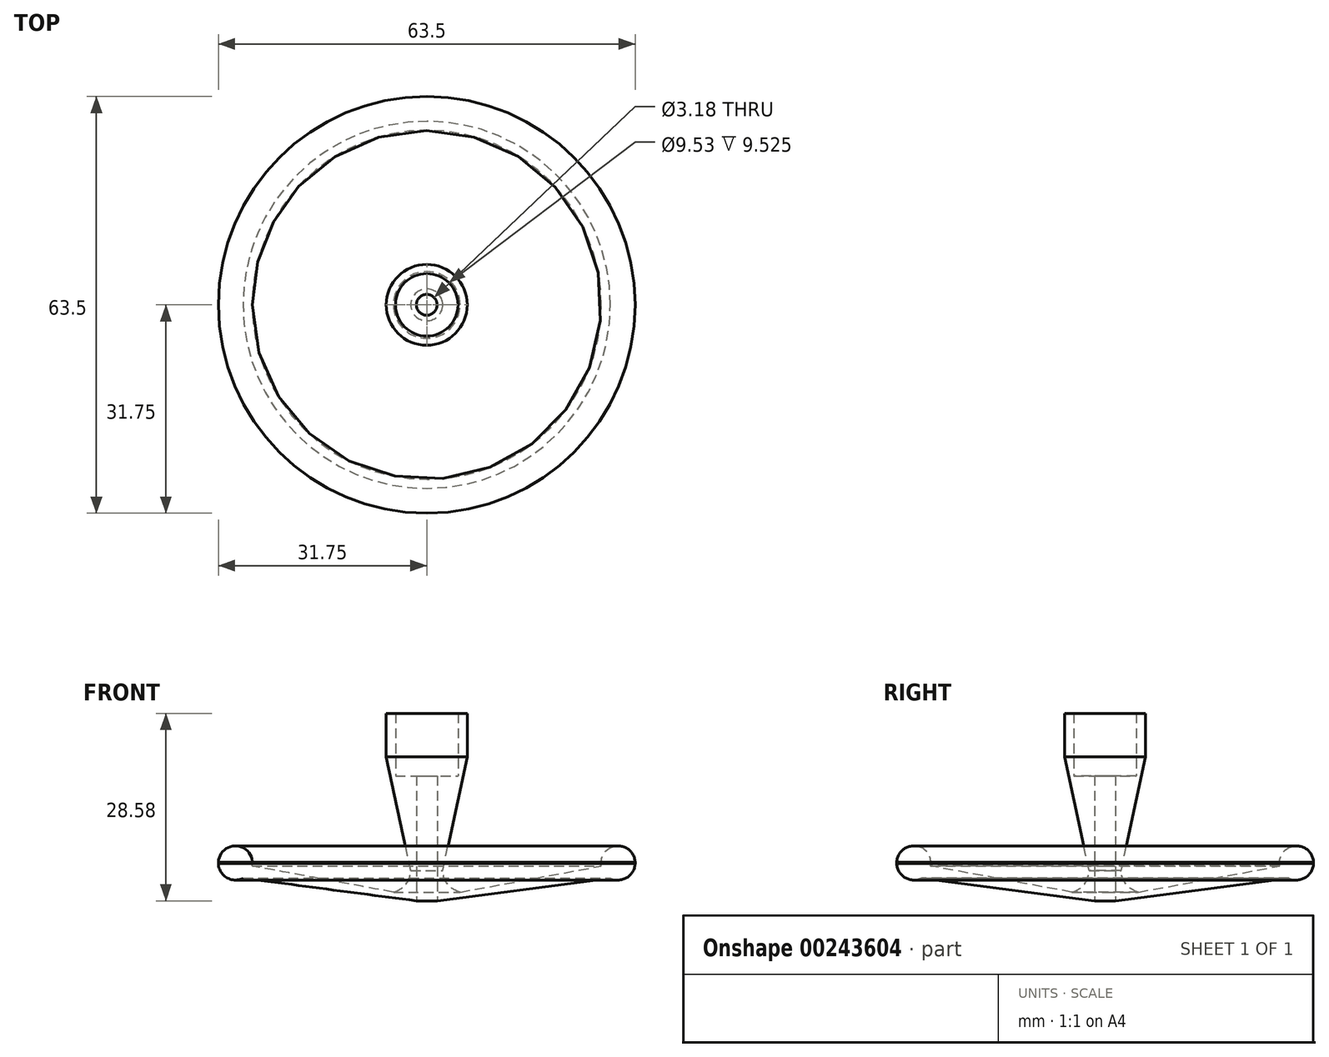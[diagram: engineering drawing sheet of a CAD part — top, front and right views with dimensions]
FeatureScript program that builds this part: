
annotation { "Feature Type Name" : "Feature", "Feature Type Description" : "" }
export const myFeature = defineFeature(function(context is Context, id is Id, definition is map)
    precondition{}
    {
        {
            var Q0;
            Q0=qCreatedBy(makeId("Front.planeOp"),FACE);
            var sketch = newSketch(context, id + "F0", { "sketchPlane" : qUnion([Q0])});
            skLineSegment(sketch, "E0.top", {"start": v(4.76, 28.58) * mm, "end": v(6.17, 28.58) * mm});
            skLineSegment(sketch, "E0.right", {"start": v(31.75, 5.66) * mm, "end": v(31.75, 5.89) * mm});
            skLineSegment(sketch, "E1.top", {"start": v(1.59, 19.05) * mm, "end": v(4.76, 19.05) * mm});
            skLineSegment(sketch, "E1.right", {"start": v(4.76, 28.58) * mm, "end": v(4.76, 19.05) * mm});
            skPoint(sketch, "E2.oppositeSnap0", {"position": v(2.38, 19.05) * mm});
            skLineSegment(sketch, "E3.bottom", {"start": v(2.38, 15.49) * mm, "end": v(2.38, 15.49) * mm});
            skLineSegment(sketch, "E3.top", {"start": v(2.38, 19.05) * mm, "end": v(2.38, 19.05) * mm});
            skLineSegment(sketch, "E4", {"start": v(1.59, 7.42) * mm, "end": v(1.59, 19.05) * mm});
            skLineSegment(sketch, "E5", {"start": v(1.59, 19.05) * mm, "end": v(1.59, 0) * mm});
            skPoint(sketch, "E1.left.end.orphan", {"position": v(0, 19.05) * mm});
            skPoint(sketch, "E6.end.orphan", {"position": v(1.59, 0.68) * mm});
            skPoint(sketch, "E7.end.orphan", {"position": v(27.94, 8.1) * mm});
            skLineSegment(sketch, "E8", {"start": v(6.17, 28.58) * mm, "end": v(6.17, 21.95) * mm});
            skLineSegment(sketch, "E9", {"start": v(6.17, 21.95) * mm, "end": v(2.43, 4.6) * mm});
            skPoint(sketch, "E10.end.orphan", {"position": v(30.36, 8.1) * mm});
            skArc(sketch, "E11", {"start": v(27.97, 3.46) * mm, "mid": v(31.2, 7.39) * mm, "end": v(26.62, 5.17) * mm});
            skPoint(sketch, "E11.first.point", {"position": v(31.75, 5.89) * mm});
            skPoint(sketch, "E11.second.point", {"position": v(26.62, 5.17) * mm});
            skPoint(sketch, "E11.third.point", {"position": v(27.97, 3.46) * mm});
            skLineSegment(sketch, "E12", {"start": v(1.59, 0) * mm, "end": v(27.97, 3.46) * mm});
            skLineSegment(sketch, "E13", {"start": v(5.08, 1.33) * mm, "end": v(26.6, 5.3) * mm});
            skArc(sketch, "E14", {"start": v(2.43, 4.6) * mm, "mid": v(3.2, 2.52) * mm, "end": v(5.08, 1.33) * mm});
            skLineSegment(sketch, "E15", {"start": v(0, 0) * mm, "end": v(0, 28.58) * mm});
            skSolve(sketch);
        }
        {
            var Q0;
            Q0=makeQuery(id+"F0.imprint","IMPRINT",FACE,{"disambiguationData":[TD([[makeQuery(id+"F0.imprint","IMPRINT",EDGE,{"derivedFrom":sQuery(id+"F0.wireOp",EDGE,"E0.top")}),-1.0]])]});
            var Q1;
            Q1=sQuery(id+"F0.wireOp",EDGE,"E15");
            revolve(context, id + "F1", {"entities" : qUnion([Q0]), "axis" : qUnion([Q1]), "revolveType" : RevolveType.FULL});
        }
    });
